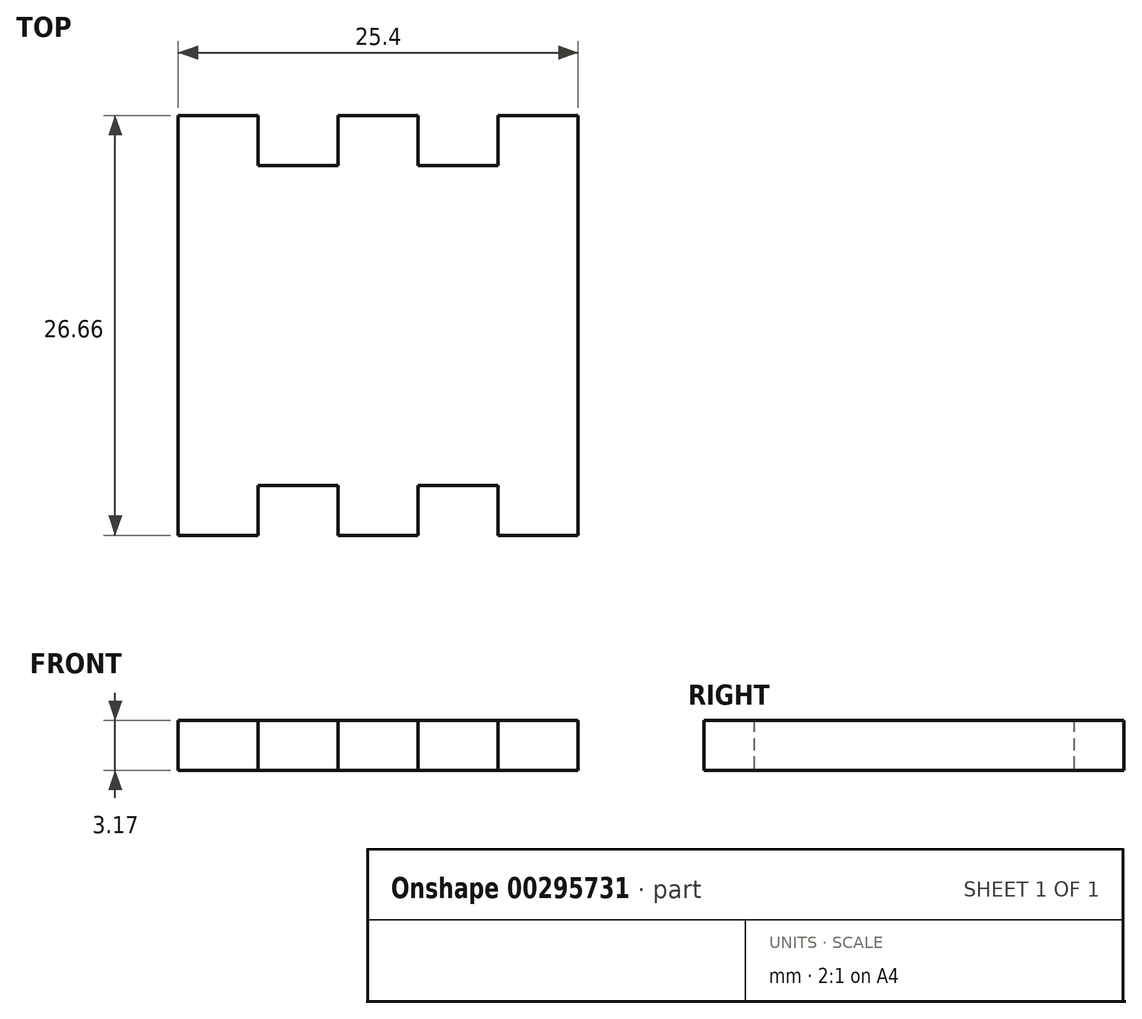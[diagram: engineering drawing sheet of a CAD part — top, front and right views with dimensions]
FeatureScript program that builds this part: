
annotation { "Feature Type Name" : "Feature", "Feature Type Description" : "" }
export const myFeature = defineFeature(function(context is Context, id is Id, definition is map)
    precondition{}
    {
        {
            var Q0;
            Q0=qCreatedBy(makeId("Top.planeOp"),FACE);
            var sketch = newSketch(context, id + "F0", { "sketchPlane" : qUnion([Q0])});
            skLineSegment(sketch, "E0.bottom", {"start": v(12.7, -13.34) * mm, "end": v(-12.7, -13.34) * mm, "construction": true});
            skPoint(sketch, "E0.middle", {"position": v(0, 0) * mm});
            skLineSegment(sketch, "E1", {"start": v(0, -13.33) * mm, "end": v(2.54, -13.33) * mm});
            skLineSegment(sketch, "E2", {"start": v(2.54, -13.34) * mm, "end": v(2.54, -10.16) * mm});
            skLineSegment(sketch, "E3", {"start": v(2.54, -10.16) * mm, "end": v(7.62, -10.16) * mm});
            skLineSegment(sketch, "E4", {"start": v(7.62, -10.16) * mm, "end": v(7.62, -13.34) * mm});
            skLineSegment(sketch, "E5", {"start": v(7.62, -13.34) * mm, "end": v(12.7, -13.33) * mm});
            skLineSegment(sketch, "E6.MirrorCS", {"start": v(-2.54, -13.34) * mm, "end": v(-2.54, -10.16) * mm});
            skLineSegment(sketch, "E7.MirrorCS", {"start": v(-2.54, -10.16) * mm, "end": v(-7.62, -10.16) * mm});
            skLineSegment(sketch, "E8.MirrorCS", {"start": v(-7.62, -10.16) * mm, "end": v(-7.62, -13.34) * mm});
            skLineSegment(sketch, "E9.MirrorCS", {"start": v(0, -13.34) * mm, "end": v(-2.54, -13.34) * mm});
            skLineSegment(sketch, "E10.MirrorCS", {"start": v(-7.62, -13.34) * mm, "end": v(-12.7, -13.34) * mm});
            skLineSegment(sketch, "E11.MirrorCS", {"start": v(-2.54, 13.34) * mm, "end": v(-2.54, 10.16) * mm});
            skLineSegment(sketch, "E12.MirrorCS", {"start": v(-2.54, 10.16) * mm, "end": v(-7.62, 10.16) * mm});
            skLineSegment(sketch, "E13.MirrorCS", {"start": v(-7.62, 13.33) * mm, "end": v(-12.7, 13.33) * mm});
            skLineSegment(sketch, "E14.MirrorCS", {"start": v(-7.62, 10.16) * mm, "end": v(-7.62, 13.34) * mm});
            skLineSegment(sketch, "E15.MirrorCS", {"start": v(0, 13.34) * mm, "end": v(-2.54, 13.34) * mm});
            skLineSegment(sketch, "E16.MirrorCS", {"start": v(7.62, 13.34) * mm, "end": v(12.7, 13.34) * mm});
            skLineSegment(sketch, "E17.MirrorCS", {"start": v(7.62, 10.16) * mm, "end": v(7.62, 13.34) * mm});
            skLineSegment(sketch, "E18.MirrorCS", {"start": v(12.7, 13.34) * mm, "end": v(-12.7, 13.33) * mm, "construction": true});
            skLineSegment(sketch, "E19.MirrorCS", {"start": v(2.54, 10.16) * mm, "end": v(7.62, 10.16) * mm});
            skLineSegment(sketch, "E20.MirrorCS", {"start": v(2.54, 13.34) * mm, "end": v(2.54, 10.16) * mm});
            skLineSegment(sketch, "E21.MirrorCS", {"start": v(0, 13.34) * mm, "end": v(2.54, 13.34) * mm});
            skLineSegment(sketch, "E22", {"start": v(-12.7, 13.33) * mm, "end": v(-12.7, -13.33) * mm});
            skLineSegment(sketch, "E23", {"start": v(12.7, 13.34) * mm, "end": v(12.7, -13.34) * mm});
            skSolve(sketch);
        }
        {
            var Q0;
            Q0 = qSketchRegion(id + "F0", true);
            extrude(context, id + "F1", {"entities" : qUnion([Q0]), "depth" : 3.17 * mm});
        }
    });
